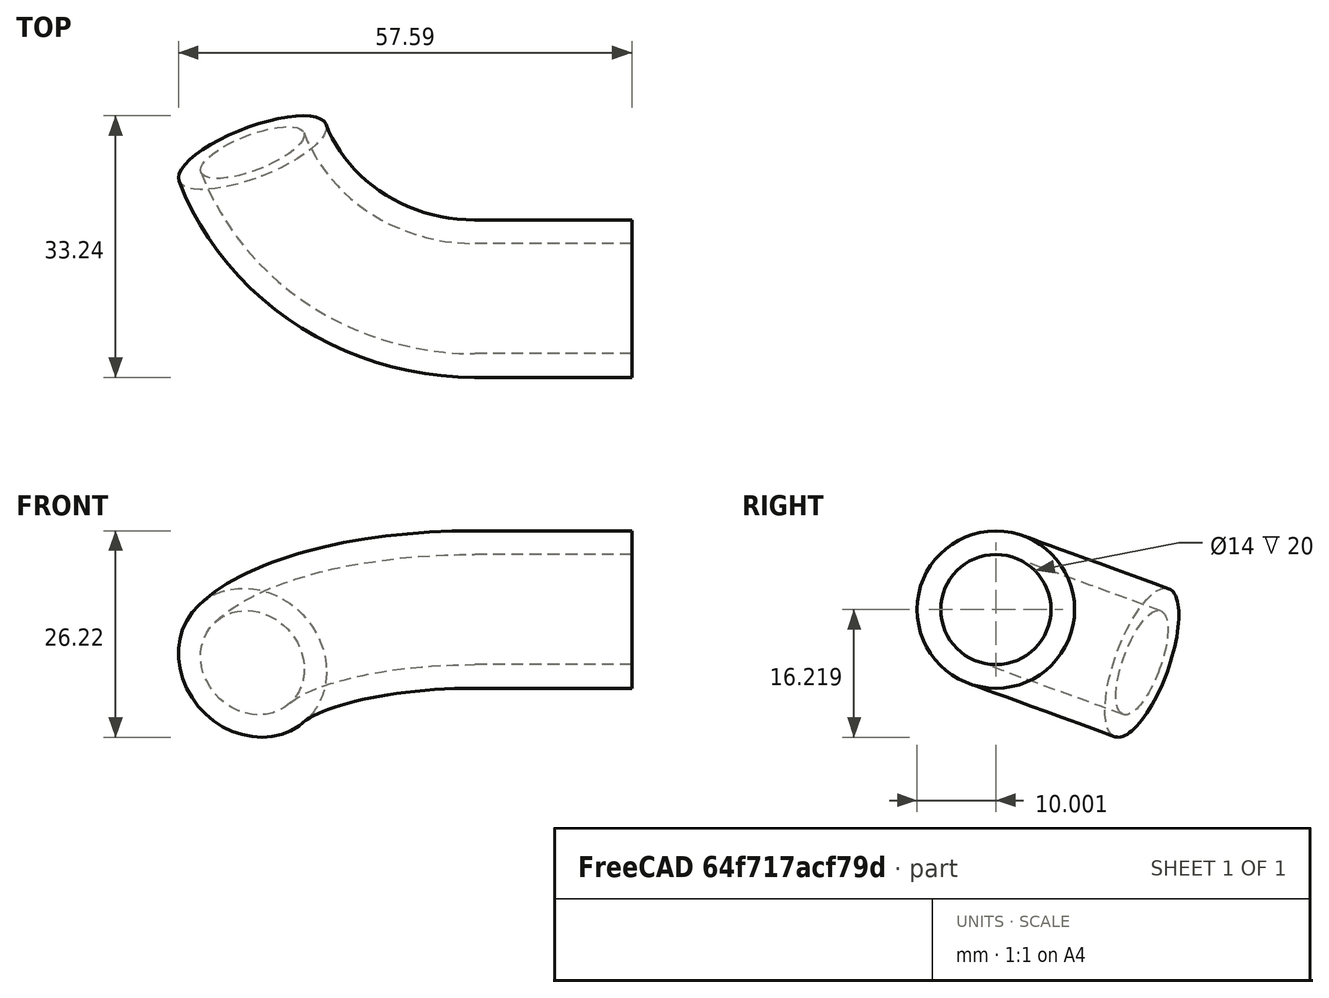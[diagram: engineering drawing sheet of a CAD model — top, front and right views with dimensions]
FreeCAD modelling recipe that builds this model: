
FCSTD DOCUMENT  (FreeCAD 0.18R4 (GitTag))
Label: cap
License: All rights reserved
LicenseURL: http://en.wikipedia.org/wiki/All_rights_reserved
objects: PartDesign::AdditiveCylinder×2, PartDesign::SubtractiveCylinder×1, PartDesign::AdditiveTorus×1, PartDesign::SubtractiveTorus×1, PartDesign::Body×1
note: 11 computed .brp shape members not serialized (recipe doc carries the construction recipe); baked Part::Feature solids carry a one-line shape summary decoded from their .brp

FEATURE [PartDesign::AdditiveCylinder] Cylinder
  Angle = 360
  AttacherType = Attacher::AttachEngine3D
  Height = 20
  Radius = 10
FEATURE [PartDesign::SubtractiveCylinder] Cylinder001
  Angle = 360
  AttacherType = Attacher::AttachEngine3D
  BaseFeature = -> Cylinder
  Height = 20
  Radius = 7
FEATURE [PartDesign::AdditiveTorus] Torus
  Angle1 = -180
  Angle2 = 180
  Angle3 = 70
  AttacherType = Attacher::AttachEngine3D
  AttachmentOffset = pos=(30,0,20) rot=(0.443713,-0.633687,0.633687;2.30637rad)
  BaseFeature = -> Cylinder001
  MapMode = 5
  Placement = pos=(30,0,20) rot=(0.443713,-0.633687,0.633687;2.30637rad)
  Radius1 = 30
  Radius2 = 10
  Support = -> [XY_Plane]
FEATURE [PartDesign::SubtractiveTorus] Torus001
  Angle1 = -180
  Angle2 = 180
  Angle3 = 70
  AttacherType = Attacher::AttachEngine3D
  AttachmentOffset = pos=(30,20,0) rot=(0,0,1;1.91986rad)
  BaseFeature = -> Torus
  MapMode = 5
  Placement = pos=(30,4.4e-15,20) rot=(0.443713,-0.633687,0.633687;2.30637rad)
  Radius1 = 30
  Radius2 = 7
  Support = -> [XZ_Plane]
FEATURE [PartDesign::AdditiveCylinder] Cylinder002
  Angle = 360
  AttacherType = Attacher::AttachEngine3D
  AttachmentOffset = pos=(0,0,14) rot=(0,0,1;0rad)
  BaseFeature = -> Torus001
  Height = 10
  MapMode = 5
  Placement = pos=(14,-3.1e-15,3.1e-15) rot=(0.57735,0.57735,0.57735;2.0944rad)
  Radius = 10
  Support = -> [YZ_Plane]
FEATURE [PartDesign::Body] Body
  Group = -> [Cylinder,Cylinder001,Torus,Torus001,Cylinder002]
  Origin = -> Origin
  Tip = -> Cylinder002
